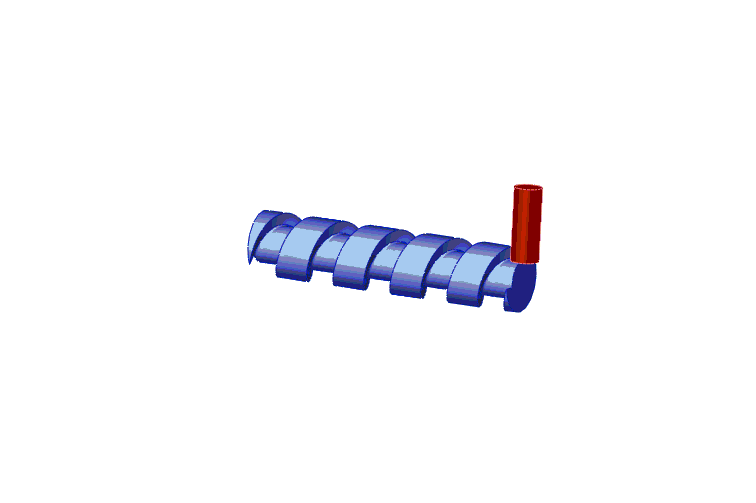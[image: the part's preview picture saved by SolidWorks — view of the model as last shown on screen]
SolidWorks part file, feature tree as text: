
SOLIDWORKS PART (.sldprt)
format: sldprt  version: not decoded by parser v0  size: 2,105,856 bytes
history: native  units: mm
features: plane x3, sketch x3, material x1, extrude x1, helix x1, revolve x1, sweep x1 (+10 scaffold rows collapsed)
feature tree (21):
  scaffold x10  (default folders/planes/origin — collapsed)
  material  "Material <not specified>"
  plane  "Front XY"
  plane  "Top XZ"
  plane  "Right YZ"
  sketch  "Sketch1"
  extrude  "Extrude1"  Depth=254mm
  sketch  "Sketch2"  dims[D1=0.0mm]
  helix  "Helix/Spiral1"  Pitch=265.715mm
  sketch  "Sketch3"
  revolve  "Revolve1"  Angle=360deg
  sweep  "Cut-Sweep1"  thickness=45.183511mm
decode coverage: 5 of 7 modeling features carry decoded parameters
note: suppression state not decoded; provenance and decode notes live in map.json
